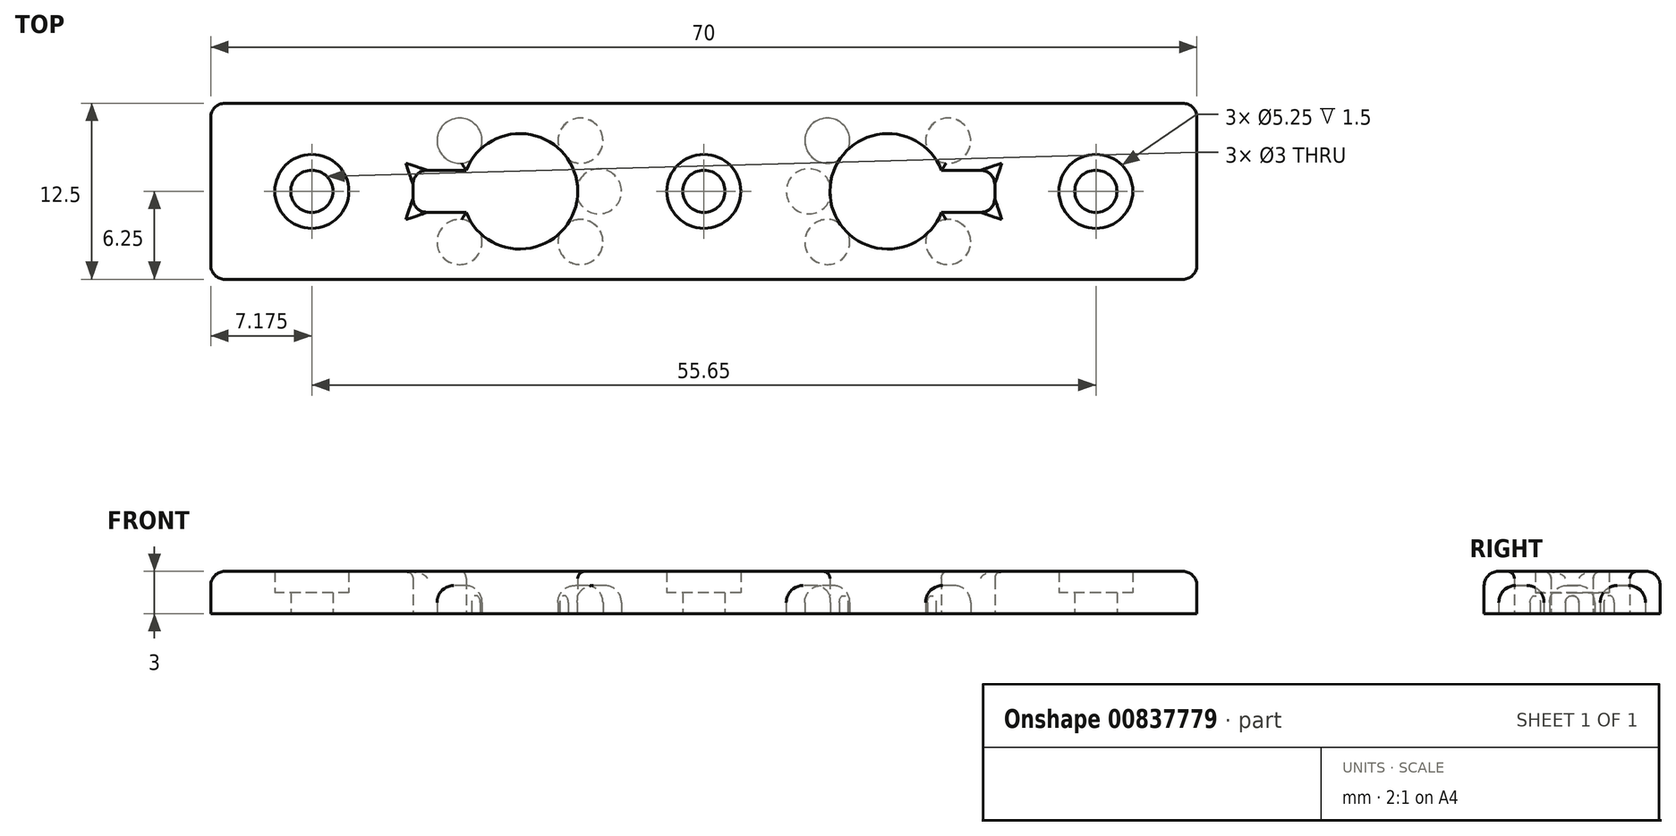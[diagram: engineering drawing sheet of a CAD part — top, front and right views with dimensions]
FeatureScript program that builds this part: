
annotation { "Feature Type Name" : "Feature", "Feature Type Description" : "" }
export const myFeature = defineFeature(function(context is Context, id is Id, definition is map)
    precondition{}
    {
        {
            var Q0;
            Q0=qCreatedBy(makeId("Top.planeOp"),FACE);
            var sketch = newSketch(context, id + "F0", { "sketchPlane" : qUnion([Q0])});
            skLineSegment(sketch, "E0.bottom", {"start": v(35, 6.25) * mm, "end": v(-35, 6.25) * mm});
            skLineSegment(sketch, "E0.top", {"start": v(35, -6.25) * mm, "end": v(-35, -6.25) * mm});
            skLineSegment(sketch, "E0.left", {"start": v(35, 6.25) * mm, "end": v(35, -6.25) * mm});
            skLineSegment(sketch, "E0.right", {"start": v(-35, 6.25) * mm, "end": v(-35, -6.25) * mm});
            skPoint(sketch, "E0.middle", {"position": v(0, 0) * mm});
            skLineSegment(sketch, "E1", {"start": v(-35, 0) * mm, "end": v(-13.05, 0) * mm, "construction": true});
            skLineSegment(sketch, "E2", {"start": v(35, 0) * mm, "end": v(13.05, 0) * mm, "construction": true});
            skCircle(sketch, "E3", {"center": v(-13.05, 0) * mm, "radius": 4.1 * mm});
            skCircle(sketch, "E4", {"center": v(13.05, 0) * mm, "radius": 4.1 * mm});
            skLineSegment(sketch, "E5", {"start": v(-13.05, 0) * mm, "end": v(-8.95, 0) * mm, "construction": true});
            skLineSegment(sketch, "E6", {"start": v(-16.2, 2.64) * mm, "end": v(-13.05, 0) * mm, "construction": true});
            skCircle(sketch, "E7", {"center": v(-13.05, 0) * mm, "radius": 4 * mm, "construction": true});
            skLineSegment(sketch, "E8", {"start": v(-17.15, 0) * mm, "end": v(-20.65, 0) * mm, "construction": true});
            skLineSegment(sketch, "E9", {"start": v(-20.65, 0) * mm, "end": v(-20.65, 1.5) * mm});
            skLineSegment(sketch, "E10", {"start": v(-20.65, 0) * mm, "end": v(-20.65, -1.5) * mm});
            skLineSegment(sketch, "E11", {"start": v(-20.65, 1.5) * mm, "end": v(-16.87, 1.5) * mm});
            skLineSegment(sketch, "E12", {"start": v(-20.65, -1.5) * mm, "end": v(-16.87, -1.5) * mm});
            skLineSegment(sketch, "E13", {"start": v(17.15, 0) * mm, "end": v(20.65, 0) * mm, "construction": true});
            skLineSegment(sketch, "E14", {"start": v(20.65, 0) * mm, "end": v(20.65, 1.5) * mm});
            skLineSegment(sketch, "E15", {"start": v(20.65, 1.5) * mm, "end": v(16.87, 1.5) * mm});
            skLineSegment(sketch, "E16", {"start": v(20.65, 0) * mm, "end": v(20.65, -1.5) * mm});
            skLineSegment(sketch, "E17", {"start": v(20.65, -1.5) * mm, "end": v(16.87, -1.5) * mm});
            skCircle(sketch, "E18", {"center": v(0, 0) * mm, "radius": 1.5 * mm});
            skLineSegment(sketch, "E19", {"start": v(-35, 0) * mm, "end": v(-27.83, 0) * mm, "construction": true});
            skLineSegment(sketch, "E20", {"start": v(35, 0) * mm, "end": v(27.83, 0) * mm, "construction": true});
            skCircle(sketch, "E21", {"center": v(27.83, 0) * mm, "radius": 1.5 * mm});
            skCircle(sketch, "E22", {"center": v(-27.83, 0) * mm, "radius": 1.5 * mm});
            skCircle(sketch, "E23", {"center": v(-27.83, 0) * mm, "radius": 2.62 * mm});
            skCircle(sketch, "E24", {"center": v(0, 0) * mm, "radius": 2.62 * mm});
            skCircle(sketch, "E25", {"center": v(27.83, 0) * mm, "radius": 2.62 * mm});
            skLineSegment(sketch, "E26", {"start": v(-16.11, 2.57) * mm, "end": v(-16.78, 3.13) * mm, "construction": true});
            skLineSegment(sketch, "E27", {"start": v(-16.11, -2.57) * mm, "end": v(-16.78, -3.13) * mm, "construction": true});
            skCircle(sketch, "E28", {"center": v(-16.78, -3.13) * mm, "radius": 0.88 * mm});
            skCircle(sketch, "E29", {"center": v(-16.78, 3.13) * mm, "radius": 0.88 * mm});
            skLineSegment(sketch, "E30", {"start": v(-13.05, 0) * mm, "end": v(-9.9, 2.64) * mm, "construction": true});
            skLineSegment(sketch, "E31", {"start": v(-13.05, 0) * mm, "end": v(-17.15, 0) * mm, "construction": true});
            skLineSegment(sketch, "E32", {"start": v(-13.05, 0) * mm, "end": v(-9.9, -2.64) * mm, "construction": true});
            skLineSegment(sketch, "E33", {"start": v(-9.99, 2.57) * mm, "end": v(-9.32, 3.13) * mm, "construction": true});
            skLineSegment(sketch, "E34", {"start": v(-9.99, -2.57) * mm, "end": v(-9.32, -3.13) * mm, "construction": true});
            skCircle(sketch, "E35", {"center": v(-9.32, -3.13) * mm, "radius": 0.88 * mm});
            skCircle(sketch, "E36", {"center": v(-9.32, 3.13) * mm, "radius": 0.88 * mm});
            skLineSegment(sketch, "E37", {"start": v(-9.05, 0) * mm, "end": v(-8.18, 0) * mm, "construction": true});
            skCircle(sketch, "E38", {"center": v(-8.18, 0) * mm, "radius": 0.88 * mm});
            skLineSegment(sketch, "E39", {"start": v(13.05, 0) * mm, "end": v(8.95, 0) * mm, "construction": true});
            skCircle(sketch, "E40", {"center": v(13.05, 0) * mm, "radius": 4 * mm, "construction": true});
            skLineSegment(sketch, "E41", {"start": v(16.11, 2.57) * mm, "end": v(16.78, 3.13) * mm, "construction": true});
            skLineSegment(sketch, "E42", {"start": v(16.11, -2.57) * mm, "end": v(16.78, -3.13) * mm, "construction": true});
            skLineSegment(sketch, "E43", {"start": v(9.05, 0) * mm, "end": v(8.18, 0) * mm, "construction": true});
            skCircle(sketch, "E44", {"center": v(8.18, 0) * mm, "radius": 0.88 * mm});
            skCircle(sketch, "E45", {"center": v(16.78, 3.13) * mm, "radius": 0.88 * mm});
            skCircle(sketch, "E46", {"center": v(16.78, -3.13) * mm, "radius": 0.88 * mm});
            skLineSegment(sketch, "E47", {"start": v(13.05, 0) * mm, "end": v(9.9, 2.64) * mm, "construction": true});
            skLineSegment(sketch, "E48", {"start": v(9.9, -2.64) * mm, "end": v(13.05, 0) * mm, "construction": true});
            skLineSegment(sketch, "E49", {"start": v(9.99, 2.57) * mm, "end": v(9.32, 3.13) * mm, "construction": true});
            skLineSegment(sketch, "E50", {"start": v(9.99, -2.57) * mm, "end": v(9.32, -3.13) * mm, "construction": true});
            skCircle(sketch, "E51", {"center": v(9.32, 3.13) * mm, "radius": 0.88 * mm});
            skCircle(sketch, "E52", {"center": v(9.32, -3.13) * mm, "radius": 0.88 * mm});
            skLineSegment(sketch, "E53", {"start": v(-16.11, -2.57) * mm, "end": v(-17.34, -3.6) * mm, "construction": true});
            skLineSegment(sketch, "E54", {"start": v(-9.99, -2.57) * mm, "end": v(-8.76, -3.6) * mm, "construction": true});
            skLineSegment(sketch, "E55", {"start": v(-9.05, 0) * mm, "end": v(-7.45, 0) * mm, "construction": true});
            skLineSegment(sketch, "E56", {"start": v(-9.99, 2.57) * mm, "end": v(-8.76, 3.6) * mm, "construction": true});
            skLineSegment(sketch, "E57", {"start": v(-16.11, 2.57) * mm, "end": v(-17.34, 3.6) * mm, "construction": true});
            skCircle(sketch, "E58", {"center": v(-17.34, -3.6) * mm, "radius": 1.6 * mm});
            skCircle(sketch, "E59", {"center": v(-8.76, -3.6) * mm, "radius": 1.6 * mm});
            skCircle(sketch, "E60", {"center": v(-7.45, 0) * mm, "radius": 1.6 * mm});
            skCircle(sketch, "E61", {"center": v(-8.76, 3.6) * mm, "radius": 1.6 * mm});
            skCircle(sketch, "E62", {"center": v(-17.34, 3.6) * mm, "radius": 1.6 * mm});
            skLineSegment(sketch, "E63", {"start": v(9.99, -2.57) * mm, "end": v(8.76, -3.6) * mm, "construction": true});
            skLineSegment(sketch, "E64", {"start": v(9.05, 0) * mm, "end": v(7.45, 0) * mm, "construction": true});
            skLineSegment(sketch, "E65", {"start": v(9.99, 2.57) * mm, "end": v(8.76, 3.6) * mm, "construction": true});
            skLineSegment(sketch, "E66", {"start": v(16.11, 2.57) * mm, "end": v(17.34, 3.6) * mm, "construction": true});
            skLineSegment(sketch, "E67", {"start": v(16.11, -2.57) * mm, "end": v(17.34, -3.6) * mm, "construction": true});
            skCircle(sketch, "E68", {"center": v(8.76, -3.6) * mm, "radius": 1.6 * mm});
            skCircle(sketch, "E69", {"center": v(7.45, 0) * mm, "radius": 1.6 * mm});
            skCircle(sketch, "E70", {"center": v(8.76, 3.6) * mm, "radius": 1.6 * mm});
            skCircle(sketch, "E71", {"center": v(17.34, 3.6) * mm, "radius": 1.6 * mm});
            skCircle(sketch, "E72", {"center": v(17.34, -3.6) * mm, "radius": 1.6 * mm});
            skSolve(sketch);
        }
        {
            var Q0;
            Q0=makeQuery(id+"F0.imprint","IMPRINT",FACE,{"disambiguationData":[TD([[makeQuery(id+"F0.imprint","IMPRINT",EDGE,{"derivedFrom":sQuery(id+"F0.wireOp",EDGE,"E0.bottom")}),1.0]])]});
            var Q1;
            Q1=makeQuery(id+"F0.imprint","IMPRINT",FACE,{"disambiguationData":[TD([[makeQuery(id+"F0.imprint","IMPRINT",EDGE,{"derivedFrom":sQuery(id+"F0.wireOp",EDGE,"E18")}),-1.0]])]});
            var Q2;
            Q2=makeQuery(id+"F0.imprint","IMPRINT",FACE,{"disambiguationData":[TD([[makeQuery(id+"F0.imprint","IMPRINT",EDGE,{"derivedFrom":sQuery(id+"F0.wireOp",EDGE,"E22")}),-1.0]])]});
            var Q3;
            Q3=makeQuery(id+"F0.imprint","IMPRINT",FACE,{"disambiguationData":[TD([[makeQuery(id+"F0.imprint","IMPRINT",EDGE,{"derivedFrom":sQuery(id+"F0.wireOp",EDGE,"E21")}),-1.0]])]});
            var Q4;
            {var subQ0=sQuery(id+"F0.wireOp",EDGE,"E29");var subQ1=sQuery(id+"F0.wireOp",EDGE,"E3");var subQ2=makeQuery(id+"F0.imprint","INTERSECT",VERTEX,{"disambiguationData":[OD(0.0)],"derivedFrom":[subQ1,subQ0]});Q4=makeQuery(id+"F0.imprint","IMPRINT",FACE,{"disambiguationData":[TD([[makeQuery(id+"F0.imprint","IMPRINT",EDGE,{"disambiguationData":[TD([[subQ2,-1.0]])],"derivedFrom":subQ1}),-1.0]])]});}
            var Q5;
            {var subQ0=sQuery(id+"F0.wireOp",EDGE,"E36");var subQ1=sQuery(id+"F0.wireOp",EDGE,"E3");var subQ2=makeQuery(id+"F0.imprint","INTERSECT",VERTEX,{"disambiguationData":[OD(0.0)],"derivedFrom":[subQ1,subQ0]});Q5=makeQuery(id+"F0.imprint","IMPRINT",FACE,{"disambiguationData":[TD([[makeQuery(id+"F0.imprint","IMPRINT",EDGE,{"disambiguationData":[TD([[subQ2,-1.0]])],"derivedFrom":subQ1}),-1.0]])]});}
            var Q6;
            {var subQ0=sQuery(id+"F0.wireOp",EDGE,"E38");var subQ1=sQuery(id+"F0.wireOp",EDGE,"E3");var subQ2=makeQuery(id+"F0.imprint","INTERSECT",VERTEX,{"disambiguationData":[OD(0.0)],"derivedFrom":[subQ1,subQ0]});Q6=makeQuery(id+"F0.imprint","IMPRINT",FACE,{"disambiguationData":[TD([[makeQuery(id+"F0.imprint","IMPRINT",EDGE,{"disambiguationData":[TD([[subQ2,1.0]])],"derivedFrom":subQ1}),-1.0]])]});}
            var Q7;
            {var subQ0=sQuery(id+"F0.wireOp",EDGE,"E28");var subQ1=sQuery(id+"F0.wireOp",EDGE,"E3");var subQ2=makeQuery(id+"F0.imprint","INTERSECT",VERTEX,{"disambiguationData":[OD(0.0)],"derivedFrom":[subQ1,subQ0]});Q7=makeQuery(id+"F0.imprint","IMPRINT",FACE,{"disambiguationData":[TD([[makeQuery(id+"F0.imprint","IMPRINT",EDGE,{"disambiguationData":[TD([[subQ2,-1.0]])],"derivedFrom":subQ1}),-1.0]])]});}
            var Q8;
            {var subQ0=sQuery(id+"F0.wireOp",EDGE,"E35");var subQ1=sQuery(id+"F0.wireOp",EDGE,"E3");var subQ2=makeQuery(id+"F0.imprint","INTERSECT",VERTEX,{"disambiguationData":[OD(0.0)],"derivedFrom":[subQ1,subQ0]});Q8=makeQuery(id+"F0.imprint","IMPRINT",FACE,{"disambiguationData":[TD([[makeQuery(id+"F0.imprint","IMPRINT",EDGE,{"disambiguationData":[TD([[subQ2,-1.0]])],"derivedFrom":subQ1}),-1.0]])]});}
            var Q9;
            {var subQ0=sQuery(id+"F0.wireOp",EDGE,"E51");var subQ1=sQuery(id+"F0.wireOp",EDGE,"E4");var subQ2=makeQuery(id+"F0.imprint","INTERSECT",VERTEX,{"disambiguationData":[OD(0.0)],"derivedFrom":[subQ1,subQ0]});Q9=makeQuery(id+"F0.imprint","IMPRINT",FACE,{"disambiguationData":[TD([[makeQuery(id+"F0.imprint","IMPRINT",EDGE,{"disambiguationData":[TD([[subQ2,-1.0]])],"derivedFrom":subQ1}),-1.0]])]});}
            var Q10;
            {var subQ0=sQuery(id+"F0.wireOp",EDGE,"E44");var subQ1=sQuery(id+"F0.wireOp",EDGE,"E4");var subQ2=makeQuery(id+"F0.imprint","INTERSECT",VERTEX,{"disambiguationData":[OD(0.0)],"derivedFrom":[subQ1,subQ0]});Q10=makeQuery(id+"F0.imprint","IMPRINT",FACE,{"disambiguationData":[TD([[makeQuery(id+"F0.imprint","IMPRINT",EDGE,{"disambiguationData":[TD([[subQ2,-1.0]])],"derivedFrom":subQ1}),-1.0]])]});}
            var Q11;
            {var subQ0=sQuery(id+"F0.wireOp",EDGE,"E52");var subQ1=sQuery(id+"F0.wireOp",EDGE,"E4");var subQ2=makeQuery(id+"F0.imprint","INTERSECT",VERTEX,{"disambiguationData":[OD(0.0)],"derivedFrom":[subQ1,subQ0]});Q11=makeQuery(id+"F0.imprint","IMPRINT",FACE,{"disambiguationData":[TD([[makeQuery(id+"F0.imprint","IMPRINT",EDGE,{"disambiguationData":[TD([[subQ2,-1.0]])],"derivedFrom":subQ1}),-1.0]])]});}
            var Q12;
            {var subQ0=sQuery(id+"F0.wireOp",EDGE,"E46");var subQ1=sQuery(id+"F0.wireOp",EDGE,"E4");var subQ2=makeQuery(id+"F0.imprint","INTERSECT",VERTEX,{"disambiguationData":[OD(0.0)],"derivedFrom":[subQ1,subQ0]});Q12=makeQuery(id+"F0.imprint","IMPRINT",FACE,{"disambiguationData":[TD([[makeQuery(id+"F0.imprint","IMPRINT",EDGE,{"disambiguationData":[TD([[subQ2,-1.0]])],"derivedFrom":subQ1}),-1.0]])]});}
            var Q13;
            {var subQ0=sQuery(id+"F0.wireOp",EDGE,"E45");var subQ1=sQuery(id+"F0.wireOp",EDGE,"E4");var subQ2=makeQuery(id+"F0.imprint","INTERSECT",VERTEX,{"disambiguationData":[OD(0.0)],"derivedFrom":[subQ1,subQ0]});Q13=makeQuery(id+"F0.imprint","IMPRINT",FACE,{"disambiguationData":[TD([[makeQuery(id+"F0.imprint","IMPRINT",EDGE,{"disambiguationData":[TD([[subQ2,-1.0]])],"derivedFrom":subQ1}),-1.0]])]});}
            var Q14;
            {var subQ0=sQuery(id+"F0.wireOp",EDGE,"VOKNR2WF-ncJ6-5r4m-VKTM-Mp244crdFX1A");var subQ1=sQuery(id+"F0.wireOp",EDGE,"E4");var subQ2=makeQuery(id+"F0.imprint","INTERSECT",VERTEX,{"disambiguationData":[OD(0.0)],"derivedFrom":[subQ1,subQ0]});Q14=makeQuery(id+"F0.imprint","IMPRINT",FACE,{"disambiguationData":[TD([[makeQuery(id+"F0.imprint","IMPRINT",EDGE,{"disambiguationData":[TD([[subQ2,-1.0]])],"derivedFrom":subQ1}),-1.0]])]});}
            var Q15;
            {var subQ0=sQuery(id+"F0.wireOp",EDGE,"JKFwxpca-5GMR-r81S-5lcH-Q0wAUQQhRcdb");var subQ1=sQuery(id+"F0.wireOp",EDGE,"E4");var subQ2=makeQuery(id+"F0.imprint","INTERSECT",VERTEX,{"disambiguationData":[OD(0.0)],"derivedFrom":[subQ1,subQ0]});Q15=makeQuery(id+"F0.imprint","IMPRINT",FACE,{"disambiguationData":[TD([[makeQuery(id+"F0.imprint","IMPRINT",EDGE,{"disambiguationData":[TD([[subQ2,-1.0]])],"derivedFrom":subQ1}),-1.0]])]});}
            var Q16;
            {var subQ0=sQuery(id+"F0.wireOp",EDGE,"RgAsl8GP-AyME-5KkZ-DOE9-8E78qrft6pB6");var subQ1=sQuery(id+"F0.wireOp",EDGE,"E4");var subQ2=makeQuery(id+"F0.imprint","INTERSECT",VERTEX,{"disambiguationData":[OD(0.0)],"derivedFrom":[subQ1,subQ0]});Q16=makeQuery(id+"F0.imprint","IMPRINT",FACE,{"disambiguationData":[TD([[makeQuery(id+"F0.imprint","IMPRINT",EDGE,{"disambiguationData":[TD([[subQ2,-1.0]])],"derivedFrom":subQ1}),-1.0]])]});}
            var Q17;
            {var subQ0=sQuery(id+"F0.wireOp",EDGE,"FUVbCvpG-FZ6w-P6KP-I0dI-AxA5oCcrSkfj");var subQ1=sQuery(id+"F0.wireOp",EDGE,"E4");var subQ2=makeQuery(id+"F0.imprint","INTERSECT",VERTEX,{"disambiguationData":[OD(0.0)],"derivedFrom":[subQ1,subQ0]});Q17=makeQuery(id+"F0.imprint","IMPRINT",FACE,{"disambiguationData":[TD([[makeQuery(id+"F0.imprint","IMPRINT",EDGE,{"disambiguationData":[TD([[subQ2,-1.0]])],"derivedFrom":subQ1}),-1.0]])]});}
            var Q18;
            {var subQ0=sQuery(id+"F0.wireOp",EDGE,"rxho1QIs-J72r-V1yP-Fany-Pfa95wKSQuel");var subQ1=sQuery(id+"F0.wireOp",EDGE,"E4");var subQ2=makeQuery(id+"F0.imprint","INTERSECT",VERTEX,{"disambiguationData":[OD(0.0)],"derivedFrom":[subQ1,subQ0]});Q18=makeQuery(id+"F0.imprint","IMPRINT",FACE,{"disambiguationData":[TD([[makeQuery(id+"F0.imprint","IMPRINT",EDGE,{"disambiguationData":[TD([[subQ2,-1.0]])],"derivedFrom":subQ1}),-1.0]])]});}
            var Q19;
            {var subQ0=sQuery(id+"F0.wireOp",EDGE,"6oBsojoL-bi50-brXo-pCNQ-iNl1vZV5s9Sy");var subQ1=sQuery(id+"F0.wireOp",EDGE,"E3");var subQ2=makeQuery(id+"F0.imprint","INTERSECT",VERTEX,{"disambiguationData":[OD(0.0)],"derivedFrom":[subQ1,subQ0]});Q19=makeQuery(id+"F0.imprint","IMPRINT",FACE,{"disambiguationData":[TD([[makeQuery(id+"F0.imprint","IMPRINT",EDGE,{"disambiguationData":[TD([[subQ2,-1.0]])],"derivedFrom":subQ1}),-1.0]])]});}
            var Q20;
            {var subQ0=sQuery(id+"F0.wireOp",EDGE,"yIff1Jyh-36eP-EJu2-z3IG-mIHMmL8X11wQ");var subQ1=sQuery(id+"F0.wireOp",EDGE,"E3");var subQ2=makeQuery(id+"F0.imprint","INTERSECT",VERTEX,{"disambiguationData":[OD(0.0)],"derivedFrom":[subQ1,subQ0]});Q20=makeQuery(id+"F0.imprint","IMPRINT",FACE,{"disambiguationData":[TD([[makeQuery(id+"F0.imprint","IMPRINT",EDGE,{"disambiguationData":[TD([[subQ2,-1.0]])],"derivedFrom":subQ1}),-1.0]])]});}
            var Q21;
            {var subQ0=sQuery(id+"F0.wireOp",EDGE,"BIAei6Qo-JPVI-veR3-2g77-xNxDojE5xRzN");var subQ1=sQuery(id+"F0.wireOp",EDGE,"E3");var subQ2=makeQuery(id+"F0.imprint","INTERSECT",VERTEX,{"disambiguationData":[OD(0.0)],"derivedFrom":[subQ1,subQ0]});Q21=makeQuery(id+"F0.imprint","IMPRINT",FACE,{"disambiguationData":[TD([[makeQuery(id+"F0.imprint","IMPRINT",EDGE,{"disambiguationData":[TD([[subQ2,-1.0]])],"derivedFrom":subQ1}),-1.0]])]});}
            var Q22;
            {var subQ0=sQuery(id+"F0.wireOp",EDGE,"AHdYGSoF-gAz6-Gu7A-dCm8-YOlxFVZfYSgz");var subQ1=sQuery(id+"F0.wireOp",EDGE,"E3");var subQ2=makeQuery(id+"F0.imprint","INTERSECT",VERTEX,{"disambiguationData":[OD(0.0)],"derivedFrom":[subQ1,subQ0]});Q22=makeQuery(id+"F0.imprint","IMPRINT",FACE,{"disambiguationData":[TD([[makeQuery(id+"F0.imprint","IMPRINT",EDGE,{"disambiguationData":[TD([[subQ2,-1.0]])],"derivedFrom":subQ1}),-1.0]])]});}
            var Q23;
            {var subQ0=sQuery(id+"F0.wireOp",EDGE,"bF5o1xas-ZAw9-uCyn-oNpS-FKpWy39mbc2z");var subQ1=sQuery(id+"F0.wireOp",EDGE,"E3");var subQ2=makeQuery(id+"F0.imprint","INTERSECT",VERTEX,{"disambiguationData":[OD(0.0)],"derivedFrom":[subQ1,subQ0]});Q23=makeQuery(id+"F0.imprint","IMPRINT",FACE,{"disambiguationData":[TD([[makeQuery(id+"F0.imprint","IMPRINT",EDGE,{"disambiguationData":[TD([[subQ2,1.0]])],"derivedFrom":subQ1}),-1.0]])]});}
            var Q24;
            {var subQ0=sQuery(id+"F0.wireOp",EDGE,"E69");var subQ1=sQuery(id+"F0.wireOp",EDGE,"E4");var subQ2=makeQuery(id+"F0.imprint","INTERSECT",VERTEX,{"disambiguationData":[OD(0.0)],"derivedFrom":[subQ1,subQ0]});Q24=makeQuery(id+"F0.imprint","IMPRINT",FACE,{"disambiguationData":[TD([[makeQuery(id+"F0.imprint","IMPRINT",EDGE,{"disambiguationData":[TD([[subQ2,-1.0]])],"derivedFrom":subQ1}),-1.0]])]});}
            var Q25;
            {var subQ0=sQuery(id+"F0.wireOp",EDGE,"E68");var subQ1=sQuery(id+"F0.wireOp",EDGE,"E4");var subQ2=makeQuery(id+"F0.imprint","INTERSECT",VERTEX,{"disambiguationData":[OD(0.0)],"derivedFrom":[subQ1,subQ0]});Q25=makeQuery(id+"F0.imprint","IMPRINT",FACE,{"disambiguationData":[TD([[makeQuery(id+"F0.imprint","IMPRINT",EDGE,{"disambiguationData":[TD([[subQ2,-1.0]])],"derivedFrom":subQ1}),-1.0]])]});}
            var Q26;
            {var subQ0=sQuery(id+"F0.wireOp",EDGE,"E72");var subQ1=sQuery(id+"F0.wireOp",EDGE,"E4");var subQ2=makeQuery(id+"F0.imprint","INTERSECT",VERTEX,{"disambiguationData":[OD(0.0)],"derivedFrom":[subQ1,subQ0]});Q26=makeQuery(id+"F0.imprint","IMPRINT",FACE,{"disambiguationData":[TD([[makeQuery(id+"F0.imprint","IMPRINT",EDGE,{"disambiguationData":[TD([[subQ2,-1.0]])],"derivedFrom":subQ1}),-1.0]])]});}
            var Q27;
            {var subQ0=sQuery(id+"F0.wireOp",EDGE,"E71");var subQ1=sQuery(id+"F0.wireOp",EDGE,"E4");var subQ2=makeQuery(id+"F0.imprint","INTERSECT",VERTEX,{"disambiguationData":[OD(0.0)],"derivedFrom":[subQ1,subQ0]});Q27=makeQuery(id+"F0.imprint","IMPRINT",FACE,{"disambiguationData":[TD([[makeQuery(id+"F0.imprint","IMPRINT",EDGE,{"disambiguationData":[TD([[subQ2,-1.0]])],"derivedFrom":subQ1}),-1.0]])]});}
            var Q28;
            {var subQ0=sQuery(id+"F0.wireOp",EDGE,"E70");var subQ1=sQuery(id+"F0.wireOp",EDGE,"E4");var subQ2=makeQuery(id+"F0.imprint","INTERSECT",VERTEX,{"disambiguationData":[OD(0.0)],"derivedFrom":[subQ1,subQ0]});Q28=makeQuery(id+"F0.imprint","IMPRINT",FACE,{"disambiguationData":[TD([[makeQuery(id+"F0.imprint","IMPRINT",EDGE,{"disambiguationData":[TD([[subQ2,-1.0]])],"derivedFrom":subQ1}),-1.0]])]});}
            var Q29;
            {var subQ0=sQuery(id+"F0.wireOp",EDGE,"E58");var subQ1=sQuery(id+"F0.wireOp",EDGE,"E3");var subQ2=makeQuery(id+"F0.imprint","INTERSECT",VERTEX,{"disambiguationData":[OD(0.0)],"derivedFrom":[subQ1,subQ0]});Q29=makeQuery(id+"F0.imprint","IMPRINT",FACE,{"disambiguationData":[TD([[makeQuery(id+"F0.imprint","IMPRINT",EDGE,{"disambiguationData":[TD([[subQ2,-1.0]])],"derivedFrom":subQ1}),-1.0]])]});}
            var Q30;
            {var subQ0=sQuery(id+"F0.wireOp",EDGE,"E62");var subQ1=sQuery(id+"F0.wireOp",EDGE,"E3");var subQ2=makeQuery(id+"F0.imprint","INTERSECT",VERTEX,{"disambiguationData":[OD(0.0)],"derivedFrom":[subQ1,subQ0]});Q30=makeQuery(id+"F0.imprint","IMPRINT",FACE,{"disambiguationData":[TD([[makeQuery(id+"F0.imprint","IMPRINT",EDGE,{"disambiguationData":[TD([[subQ2,-1.0]])],"derivedFrom":subQ1}),-1.0]])]});}
            var Q31;
            {var subQ0=sQuery(id+"F0.wireOp",EDGE,"E61");var subQ1=sQuery(id+"F0.wireOp",EDGE,"E3");var subQ2=makeQuery(id+"F0.imprint","INTERSECT",VERTEX,{"disambiguationData":[OD(0.0)],"derivedFrom":[subQ1,subQ0]});Q31=makeQuery(id+"F0.imprint","IMPRINT",FACE,{"disambiguationData":[TD([[makeQuery(id+"F0.imprint","IMPRINT",EDGE,{"disambiguationData":[TD([[subQ2,-1.0]])],"derivedFrom":subQ1}),-1.0]])]});}
            var Q32;
            {var subQ0=sQuery(id+"F0.wireOp",EDGE,"E60");var subQ1=sQuery(id+"F0.wireOp",EDGE,"E3");var subQ2=makeQuery(id+"F0.imprint","INTERSECT",VERTEX,{"disambiguationData":[OD(0.0)],"derivedFrom":[subQ1,subQ0]});Q32=makeQuery(id+"F0.imprint","IMPRINT",FACE,{"disambiguationData":[TD([[makeQuery(id+"F0.imprint","IMPRINT",EDGE,{"disambiguationData":[TD([[subQ2,1.0]])],"derivedFrom":subQ1}),-1.0]])]});}
            var Q33;
            {var subQ0=sQuery(id+"F0.wireOp",EDGE,"E59");var subQ1=sQuery(id+"F0.wireOp",EDGE,"E3");var subQ2=makeQuery(id+"F0.imprint","INTERSECT",VERTEX,{"disambiguationData":[OD(0.0)],"derivedFrom":[subQ1,subQ0]});Q33=makeQuery(id+"F0.imprint","IMPRINT",FACE,{"disambiguationData":[TD([[makeQuery(id+"F0.imprint","IMPRINT",EDGE,{"disambiguationData":[TD([[subQ2,-1.0]])],"derivedFrom":subQ1}),-1.0]])]});}
            extrude(context, id + "F1", {"entities" : qUnion([Q0, Q1, Q2, Q3, Q4, Q5, Q6, Q7, Q8, Q9, Q10, Q11, Q12, Q13, Q14, Q15, Q16, Q17, Q18, Q19, Q20, Q21, Q22, Q23, Q24, Q25, Q26, Q27, Q28, Q29, Q30, Q31, Q32, Q33]), "depth" : 3 * mm, "offsetDistance" : 25 * mm});
        }
        {
            var Q0;
            {var subQ0=sQuery(id+"F0.wireOp",EDGE,"E28");var subQ1=sQuery(id+"F0.wireOp",EDGE,"E3");var subQ2=makeQuery(id+"F0.imprint","INTERSECT",VERTEX,{"disambiguationData":[OD(0.0)],"derivedFrom":[subQ1,subQ0]});Q0=makeQuery(id+"F0.imprint","IMPRINT",FACE,{"disambiguationData":[TD([[makeQuery(id+"F0.imprint","IMPRINT",EDGE,{"disambiguationData":[TD([[subQ2,-1.0]])],"derivedFrom":subQ1}),-1.0]])]});}
            var Q1;
            {var subQ0=sQuery(id+"F0.wireOp",EDGE,"E29");var subQ1=sQuery(id+"F0.wireOp",EDGE,"E3");var subQ2=makeQuery(id+"F0.imprint","INTERSECT",VERTEX,{"disambiguationData":[OD(0.0)],"derivedFrom":[subQ1,subQ0]});Q1=makeQuery(id+"F0.imprint","IMPRINT",FACE,{"disambiguationData":[TD([[makeQuery(id+"F0.imprint","IMPRINT",EDGE,{"disambiguationData":[TD([[subQ2,-1.0]])],"derivedFrom":subQ1}),-1.0]])]});}
            var Q2;
            {var subQ0=sQuery(id+"F0.wireOp",EDGE,"E36");var subQ1=sQuery(id+"F0.wireOp",EDGE,"E3");var subQ2=makeQuery(id+"F0.imprint","INTERSECT",VERTEX,{"disambiguationData":[OD(0.0)],"derivedFrom":[subQ1,subQ0]});Q2=makeQuery(id+"F0.imprint","IMPRINT",FACE,{"disambiguationData":[TD([[makeQuery(id+"F0.imprint","IMPRINT",EDGE,{"disambiguationData":[TD([[subQ2,-1.0]])],"derivedFrom":subQ1}),-1.0]])]});}
            var Q3;
            {var subQ0=sQuery(id+"F0.wireOp",EDGE,"E38");var subQ1=sQuery(id+"F0.wireOp",EDGE,"E3");var subQ2=makeQuery(id+"F0.imprint","INTERSECT",VERTEX,{"disambiguationData":[OD(0.0)],"derivedFrom":[subQ1,subQ0]});Q3=makeQuery(id+"F0.imprint","IMPRINT",FACE,{"disambiguationData":[TD([[makeQuery(id+"F0.imprint","IMPRINT",EDGE,{"disambiguationData":[TD([[subQ2,1.0]])],"derivedFrom":subQ1}),-1.0]])]});}
            var Q4;
            {var subQ0=sQuery(id+"F0.wireOp",EDGE,"E35");var subQ1=sQuery(id+"F0.wireOp",EDGE,"E3");var subQ2=makeQuery(id+"F0.imprint","INTERSECT",VERTEX,{"disambiguationData":[OD(0.0)],"derivedFrom":[subQ1,subQ0]});Q4=makeQuery(id+"F0.imprint","IMPRINT",FACE,{"disambiguationData":[TD([[makeQuery(id+"F0.imprint","IMPRINT",EDGE,{"disambiguationData":[TD([[subQ2,-1.0]])],"derivedFrom":subQ1}),-1.0]])]});}
            var Q5;
            {var subQ0=sQuery(id+"F0.wireOp",EDGE,"E52");var subQ1=sQuery(id+"F0.wireOp",EDGE,"E4");var subQ2=makeQuery(id+"F0.imprint","INTERSECT",VERTEX,{"disambiguationData":[OD(0.0)],"derivedFrom":[subQ1,subQ0]});Q5=makeQuery(id+"F0.imprint","IMPRINT",FACE,{"disambiguationData":[TD([[makeQuery(id+"F0.imprint","IMPRINT",EDGE,{"disambiguationData":[TD([[subQ2,-1.0]])],"derivedFrom":subQ1}),-1.0]])]});}
            var Q6;
            {var subQ0=sQuery(id+"F0.wireOp",EDGE,"E44");var subQ1=sQuery(id+"F0.wireOp",EDGE,"E4");var subQ2=makeQuery(id+"F0.imprint","INTERSECT",VERTEX,{"disambiguationData":[OD(0.0)],"derivedFrom":[subQ1,subQ0]});Q6=makeQuery(id+"F0.imprint","IMPRINT",FACE,{"disambiguationData":[TD([[makeQuery(id+"F0.imprint","IMPRINT",EDGE,{"disambiguationData":[TD([[subQ2,-1.0]])],"derivedFrom":subQ1}),-1.0]])]});}
            var Q7;
            {var subQ0=sQuery(id+"F0.wireOp",EDGE,"E51");var subQ1=sQuery(id+"F0.wireOp",EDGE,"E4");var subQ2=makeQuery(id+"F0.imprint","INTERSECT",VERTEX,{"disambiguationData":[OD(0.0)],"derivedFrom":[subQ1,subQ0]});Q7=makeQuery(id+"F0.imprint","IMPRINT",FACE,{"disambiguationData":[TD([[makeQuery(id+"F0.imprint","IMPRINT",EDGE,{"disambiguationData":[TD([[subQ2,-1.0]])],"derivedFrom":subQ1}),-1.0]])]});}
            var Q8;
            {var subQ0=sQuery(id+"F0.wireOp",EDGE,"E46");var subQ1=sQuery(id+"F0.wireOp",EDGE,"E4");var subQ2=makeQuery(id+"F0.imprint","INTERSECT",VERTEX,{"disambiguationData":[OD(0.0)],"derivedFrom":[subQ1,subQ0]});Q8=makeQuery(id+"F0.imprint","IMPRINT",FACE,{"disambiguationData":[TD([[makeQuery(id+"F0.imprint","IMPRINT",EDGE,{"disambiguationData":[TD([[subQ2,-1.0]])],"derivedFrom":subQ1}),-1.0]])]});}
            var Q9;
            {var subQ0=sQuery(id+"F0.wireOp",EDGE,"E45");var subQ1=sQuery(id+"F0.wireOp",EDGE,"E4");var subQ2=makeQuery(id+"F0.imprint","INTERSECT",VERTEX,{"disambiguationData":[OD(0.0)],"derivedFrom":[subQ1,subQ0]});Q9=makeQuery(id+"F0.imprint","IMPRINT",FACE,{"disambiguationData":[TD([[makeQuery(id+"F0.imprint","IMPRINT",EDGE,{"disambiguationData":[TD([[subQ2,-1.0]])],"derivedFrom":subQ1}),-1.0]])]});}
            var Q10;
            {var subQ0=sQuery(id+"F0.wireOp",EDGE,"yIff1Jyh-36eP-EJu2-z3IG-mIHMmL8X11wQ");var subQ1=sQuery(id+"F0.wireOp",EDGE,"E3");var subQ2=makeQuery(id+"F0.imprint","INTERSECT",VERTEX,{"disambiguationData":[OD(0.0)],"derivedFrom":[subQ1,subQ0]});Q10=makeQuery(id+"F0.imprint","IMPRINT",FACE,{"disambiguationData":[TD([[makeQuery(id+"F0.imprint","IMPRINT",EDGE,{"disambiguationData":[TD([[subQ2,-1.0]])],"derivedFrom":subQ1}),-1.0]])]});}
            var Q11;
            {var subQ0=sQuery(id+"F0.wireOp",EDGE,"6oBsojoL-bi50-brXo-pCNQ-iNl1vZV5s9Sy");var subQ1=sQuery(id+"F0.wireOp",EDGE,"E3");var subQ2=makeQuery(id+"F0.imprint","INTERSECT",VERTEX,{"disambiguationData":[OD(0.0)],"derivedFrom":[subQ1,subQ0]});Q11=makeQuery(id+"F0.imprint","IMPRINT",FACE,{"disambiguationData":[TD([[makeQuery(id+"F0.imprint","IMPRINT",EDGE,{"disambiguationData":[TD([[subQ2,-1.0]])],"derivedFrom":subQ1}),-1.0]])]});}
            var Q12;
            {var subQ0=sQuery(id+"F0.wireOp",EDGE,"bF5o1xas-ZAw9-uCyn-oNpS-FKpWy39mbc2z");var subQ1=sQuery(id+"F0.wireOp",EDGE,"E3");var subQ2=makeQuery(id+"F0.imprint","INTERSECT",VERTEX,{"disambiguationData":[OD(0.0)],"derivedFrom":[subQ1,subQ0]});Q12=makeQuery(id+"F0.imprint","IMPRINT",FACE,{"disambiguationData":[TD([[makeQuery(id+"F0.imprint","IMPRINT",EDGE,{"disambiguationData":[TD([[subQ2,1.0]])],"derivedFrom":subQ1}),-1.0]])]});}
            var Q13;
            {var subQ0=sQuery(id+"F0.wireOp",EDGE,"AHdYGSoF-gAz6-Gu7A-dCm8-YOlxFVZfYSgz");var subQ1=sQuery(id+"F0.wireOp",EDGE,"E3");var subQ2=makeQuery(id+"F0.imprint","INTERSECT",VERTEX,{"disambiguationData":[OD(0.0)],"derivedFrom":[subQ1,subQ0]});Q13=makeQuery(id+"F0.imprint","IMPRINT",FACE,{"disambiguationData":[TD([[makeQuery(id+"F0.imprint","IMPRINT",EDGE,{"disambiguationData":[TD([[subQ2,-1.0]])],"derivedFrom":subQ1}),-1.0]])]});}
            var Q14;
            {var subQ0=sQuery(id+"F0.wireOp",EDGE,"BIAei6Qo-JPVI-veR3-2g77-xNxDojE5xRzN");var subQ1=sQuery(id+"F0.wireOp",EDGE,"E3");var subQ2=makeQuery(id+"F0.imprint","INTERSECT",VERTEX,{"disambiguationData":[OD(0.0)],"derivedFrom":[subQ1,subQ0]});Q14=makeQuery(id+"F0.imprint","IMPRINT",FACE,{"disambiguationData":[TD([[makeQuery(id+"F0.imprint","IMPRINT",EDGE,{"disambiguationData":[TD([[subQ2,-1.0]])],"derivedFrom":subQ1}),-1.0]])]});}
            var Q15;
            {var subQ0=sQuery(id+"F0.wireOp",EDGE,"VOKNR2WF-ncJ6-5r4m-VKTM-Mp244crdFX1A");var subQ1=sQuery(id+"F0.wireOp",EDGE,"E4");var subQ2=makeQuery(id+"F0.imprint","INTERSECT",VERTEX,{"disambiguationData":[OD(0.0)],"derivedFrom":[subQ1,subQ0]});Q15=makeQuery(id+"F0.imprint","IMPRINT",FACE,{"disambiguationData":[TD([[makeQuery(id+"F0.imprint","IMPRINT",EDGE,{"disambiguationData":[TD([[subQ2,-1.0]])],"derivedFrom":subQ1}),-1.0]])]});}
            var Q16;
            {var subQ0=sQuery(id+"F0.wireOp",EDGE,"rxho1QIs-J72r-V1yP-Fany-Pfa95wKSQuel");var subQ1=sQuery(id+"F0.wireOp",EDGE,"E4");var subQ2=makeQuery(id+"F0.imprint","INTERSECT",VERTEX,{"disambiguationData":[OD(0.0)],"derivedFrom":[subQ1,subQ0]});Q16=makeQuery(id+"F0.imprint","IMPRINT",FACE,{"disambiguationData":[TD([[makeQuery(id+"F0.imprint","IMPRINT",EDGE,{"disambiguationData":[TD([[subQ2,-1.0]])],"derivedFrom":subQ1}),-1.0]])]});}
            var Q17;
            {var subQ0=sQuery(id+"F0.wireOp",EDGE,"FUVbCvpG-FZ6w-P6KP-I0dI-AxA5oCcrSkfj");var subQ1=sQuery(id+"F0.wireOp",EDGE,"E4");var subQ2=makeQuery(id+"F0.imprint","INTERSECT",VERTEX,{"disambiguationData":[OD(0.0)],"derivedFrom":[subQ1,subQ0]});Q17=makeQuery(id+"F0.imprint","IMPRINT",FACE,{"disambiguationData":[TD([[makeQuery(id+"F0.imprint","IMPRINT",EDGE,{"disambiguationData":[TD([[subQ2,-1.0]])],"derivedFrom":subQ1}),-1.0]])]});}
            var Q18;
            {var subQ0=sQuery(id+"F0.wireOp",EDGE,"RgAsl8GP-AyME-5KkZ-DOE9-8E78qrft6pB6");var subQ1=sQuery(id+"F0.wireOp",EDGE,"E4");var subQ2=makeQuery(id+"F0.imprint","INTERSECT",VERTEX,{"disambiguationData":[OD(0.0)],"derivedFrom":[subQ1,subQ0]});Q18=makeQuery(id+"F0.imprint","IMPRINT",FACE,{"disambiguationData":[TD([[makeQuery(id+"F0.imprint","IMPRINT",EDGE,{"disambiguationData":[TD([[subQ2,-1.0]])],"derivedFrom":subQ1}),-1.0]])]});}
            var Q19;
            {var subQ0=sQuery(id+"F0.wireOp",EDGE,"JKFwxpca-5GMR-r81S-5lcH-Q0wAUQQhRcdb");var subQ1=sQuery(id+"F0.wireOp",EDGE,"E4");var subQ2=makeQuery(id+"F0.imprint","INTERSECT",VERTEX,{"disambiguationData":[OD(0.0)],"derivedFrom":[subQ1,subQ0]});Q19=makeQuery(id+"F0.imprint","IMPRINT",FACE,{"disambiguationData":[TD([[makeQuery(id+"F0.imprint","IMPRINT",EDGE,{"disambiguationData":[TD([[subQ2,-1.0]])],"derivedFrom":subQ1}),-1.0]])]});}
            var Q20;
            {var subQ0=sQuery(id+"F0.wireOp",EDGE,"E58");var subQ1=sQuery(id+"F0.wireOp",EDGE,"E3");var subQ2=makeQuery(id+"F0.imprint","INTERSECT",VERTEX,{"disambiguationData":[OD(0.0)],"derivedFrom":[subQ1,subQ0]});Q20=makeQuery(id+"F0.imprint","IMPRINT",FACE,{"disambiguationData":[TD([[makeQuery(id+"F0.imprint","IMPRINT",EDGE,{"disambiguationData":[TD([[subQ2,-1.0]])],"derivedFrom":subQ1}),-1.0]])]});}
            var Q21;
            {var subQ0=sQuery(id+"F0.wireOp",EDGE,"E59");var subQ1=sQuery(id+"F0.wireOp",EDGE,"E3");var subQ2=makeQuery(id+"F0.imprint","INTERSECT",VERTEX,{"disambiguationData":[OD(0.0)],"derivedFrom":[subQ1,subQ0]});Q21=makeQuery(id+"F0.imprint","IMPRINT",FACE,{"disambiguationData":[TD([[makeQuery(id+"F0.imprint","IMPRINT",EDGE,{"disambiguationData":[TD([[subQ2,-1.0]])],"derivedFrom":subQ1}),-1.0]])]});}
            var Q22;
            {var subQ0=sQuery(id+"F0.wireOp",EDGE,"E60");var subQ1=sQuery(id+"F0.wireOp",EDGE,"E3");var subQ2=makeQuery(id+"F0.imprint","INTERSECT",VERTEX,{"disambiguationData":[OD(0.0)],"derivedFrom":[subQ1,subQ0]});Q22=makeQuery(id+"F0.imprint","IMPRINT",FACE,{"disambiguationData":[TD([[makeQuery(id+"F0.imprint","IMPRINT",EDGE,{"disambiguationData":[TD([[subQ2,1.0]])],"derivedFrom":subQ1}),-1.0]])]});}
            var Q23;
            {var subQ0=sQuery(id+"F0.wireOp",EDGE,"E61");var subQ1=sQuery(id+"F0.wireOp",EDGE,"E3");var subQ2=makeQuery(id+"F0.imprint","INTERSECT",VERTEX,{"disambiguationData":[OD(0.0)],"derivedFrom":[subQ1,subQ0]});Q23=makeQuery(id+"F0.imprint","IMPRINT",FACE,{"disambiguationData":[TD([[makeQuery(id+"F0.imprint","IMPRINT",EDGE,{"disambiguationData":[TD([[subQ2,-1.0]])],"derivedFrom":subQ1}),-1.0]])]});}
            var Q24;
            {var subQ0=sQuery(id+"F0.wireOp",EDGE,"E62");var subQ1=sQuery(id+"F0.wireOp",EDGE,"E3");var subQ2=makeQuery(id+"F0.imprint","INTERSECT",VERTEX,{"disambiguationData":[OD(0.0)],"derivedFrom":[subQ1,subQ0]});Q24=makeQuery(id+"F0.imprint","IMPRINT",FACE,{"disambiguationData":[TD([[makeQuery(id+"F0.imprint","IMPRINT",EDGE,{"disambiguationData":[TD([[subQ2,-1.0]])],"derivedFrom":subQ1}),-1.0]])]});}
            var Q25;
            {var subQ0=sQuery(id+"F0.wireOp",EDGE,"E72");var subQ1=sQuery(id+"F0.wireOp",EDGE,"E4");var subQ2=makeQuery(id+"F0.imprint","INTERSECT",VERTEX,{"disambiguationData":[OD(0.0)],"derivedFrom":[subQ1,subQ0]});Q25=makeQuery(id+"F0.imprint","IMPRINT",FACE,{"disambiguationData":[TD([[makeQuery(id+"F0.imprint","IMPRINT",EDGE,{"disambiguationData":[TD([[subQ2,-1.0]])],"derivedFrom":subQ1}),-1.0]])]});}
            var Q26;
            {var subQ0=sQuery(id+"F0.wireOp",EDGE,"E68");var subQ1=sQuery(id+"F0.wireOp",EDGE,"E4");var subQ2=makeQuery(id+"F0.imprint","INTERSECT",VERTEX,{"disambiguationData":[OD(0.0)],"derivedFrom":[subQ1,subQ0]});Q26=makeQuery(id+"F0.imprint","IMPRINT",FACE,{"disambiguationData":[TD([[makeQuery(id+"F0.imprint","IMPRINT",EDGE,{"disambiguationData":[TD([[subQ2,-1.0]])],"derivedFrom":subQ1}),-1.0]])]});}
            var Q27;
            {var subQ0=sQuery(id+"F0.wireOp",EDGE,"E69");var subQ1=sQuery(id+"F0.wireOp",EDGE,"E4");var subQ2=makeQuery(id+"F0.imprint","INTERSECT",VERTEX,{"disambiguationData":[OD(0.0)],"derivedFrom":[subQ1,subQ0]});Q27=makeQuery(id+"F0.imprint","IMPRINT",FACE,{"disambiguationData":[TD([[makeQuery(id+"F0.imprint","IMPRINT",EDGE,{"disambiguationData":[TD([[subQ2,-1.0]])],"derivedFrom":subQ1}),-1.0]])]});}
            var Q28;
            {var subQ0=sQuery(id+"F0.wireOp",EDGE,"E70");var subQ1=sQuery(id+"F0.wireOp",EDGE,"E4");var subQ2=makeQuery(id+"F0.imprint","INTERSECT",VERTEX,{"disambiguationData":[OD(0.0)],"derivedFrom":[subQ1,subQ0]});Q28=makeQuery(id+"F0.imprint","IMPRINT",FACE,{"disambiguationData":[TD([[makeQuery(id+"F0.imprint","IMPRINT",EDGE,{"disambiguationData":[TD([[subQ2,-1.0]])],"derivedFrom":subQ1}),-1.0]])]});}
            var Q29;
            {var subQ0=sQuery(id+"F0.wireOp",EDGE,"E71");var subQ1=sQuery(id+"F0.wireOp",EDGE,"E4");var subQ2=makeQuery(id+"F0.imprint","INTERSECT",VERTEX,{"disambiguationData":[OD(0.0)],"derivedFrom":[subQ1,subQ0]});Q29=makeQuery(id+"F0.imprint","IMPRINT",FACE,{"disambiguationData":[TD([[makeQuery(id+"F0.imprint","IMPRINT",EDGE,{"disambiguationData":[TD([[subQ2,-1.0]])],"derivedFrom":subQ1}),-1.0]])]});}
            extrude(context, id + "F2", {"entities" : qUnion([Q0, Q1, Q2, Q3, Q4, Q5, Q6, Q7, Q8, Q9, Q10, Q11, Q12, Q13, Q14, Q15, Q16, Q17, Q18, Q19, Q20, Q21, Q22, Q23, Q24, Q25, Q26, Q27, Q28, Q29]), "operationType" : NewBodyOperationType.REMOVE, "depth" : 2 * mm, "offsetDistance" : 25 * mm});
        }
        {
            var Q0;
            Q0=makeQuery(id+"F0.imprint","IMPRINT",FACE,{"disambiguationData":[TD([[makeQuery(id+"F0.imprint","IMPRINT",EDGE,{"derivedFrom":sQuery(id+"F0.wireOp",EDGE,"E22")}),-1.0]])]});
            var Q1;
            Q1=makeQuery(id+"F0.imprint","IMPRINT",FACE,{"disambiguationData":[TD([[makeQuery(id+"F0.imprint","IMPRINT",EDGE,{"derivedFrom":sQuery(id+"F0.wireOp",EDGE,"E18")}),-1.0]])]});
            var Q2;
            Q2=makeQuery(id+"F0.imprint","IMPRINT",FACE,{"disambiguationData":[TD([[makeQuery(id+"F0.imprint","IMPRINT",EDGE,{"derivedFrom":sQuery(id+"F0.wireOp",EDGE,"E21")}),-1.0]])]});
            extrude(context, id + "F3", {"entities" : qUnion([Q0, Q1, Q2]), "operationType" : NewBodyOperationType.REMOVE, "depth" : 3 * mm, "offsetDistance" : 25 * mm});
        }
        {
            var Q0;
            Q0=makeQuery(id+"F0.imprint","IMPRINT",FACE,{"disambiguationData":[TD([[makeQuery(id+"F0.imprint","IMPRINT",EDGE,{"derivedFrom":sQuery(id+"F0.wireOp",EDGE,"E22")}),-1.0]])]});
            var Q1;
            Q1=makeQuery(id+"F0.imprint","IMPRINT",FACE,{"disambiguationData":[TD([[makeQuery(id+"F0.imprint","IMPRINT",EDGE,{"derivedFrom":sQuery(id+"F0.wireOp",EDGE,"E18")}),-1.0]])]});
            var Q2;
            Q2=makeQuery(id+"F0.imprint","IMPRINT",FACE,{"disambiguationData":[TD([[makeQuery(id+"F0.imprint","IMPRINT",EDGE,{"derivedFrom":sQuery(id+"F0.wireOp",EDGE,"E21")}),-1.0]])]});
            extrude(context, id + "F4", {"entities" : qUnion([Q0, Q1, Q2]), "operationType" : NewBodyOperationType.ADD, "depth" : 1.5 * mm, "offsetDistance" : 25 * mm});
        }
        {
            var Q0;
            Q0=makeQuery(id+"F1.opExtrude","CAP_EDGE",EDGE,{"disambiguationData":[OSD([sQuery(id+"F0.wireOp",EDGE,"E0.left")])],"isStart":false});
            var Q1;
            Q1=makeQuery(id+"F1.opExtrude","SWEPT_EDGE",EDGE,{"disambiguationData":[OSD([sQuery(id+"F0.wireOp",EDGE,"E0.bottom"),sQuery(id+"F0.wireOp",EDGE,"E0.left")])]});
            var Q2;
            Q2=makeQuery(id+"F1.opExtrude","CAP_EDGE",EDGE,{"disambiguationData":[OSD([sQuery(id+"F0.wireOp",EDGE,"E0.bottom")])],"isStart":false});
            var Q3;
            Q3=makeQuery(id+"F1.opExtrude","CAP_EDGE",EDGE,{"disambiguationData":[OSD([sQuery(id+"F0.wireOp",EDGE,"E0.top")])],"isStart":false});
            var Q4;
            Q4=makeQuery(id+"F1.opExtrude","SWEPT_EDGE",EDGE,{"disambiguationData":[OSD([sQuery(id+"F0.wireOp",EDGE,"E0.top"),sQuery(id+"F0.wireOp",EDGE,"E0.right")])]});
            var Q5;
            Q5=makeQuery(id+"F1.opExtrude","CAP_EDGE",EDGE,{"disambiguationData":[OSD([sQuery(id+"F0.wireOp",EDGE,"E0.right")])],"isStart":false});
            var Q6;
            Q6=makeQuery(id+"F1.opExtrude","SWEPT_EDGE",EDGE,{"disambiguationData":[OSD([sQuery(id+"F0.wireOp",EDGE,"E0.bottom"),sQuery(id+"F0.wireOp",EDGE,"E0.right")])]});
            var Q7;
            Q7=makeQuery(id+"F1.opExtrude","SWEPT_EDGE",EDGE,{"disambiguationData":[OSD([sQuery(id+"F0.wireOp",EDGE,"E0.top"),sQuery(id+"F0.wireOp",EDGE,"E0.left")])]});
            fillet(context, id + "F5", {"entities" : qUnion([Q0, Q1, Q2, Q3, Q4, Q5, Q6, Q7]), "radius" : 1 * mm, "tangentPropagation" : true, "allowEdgeOverflow" : false});
        }
        {
            var Q0;
            Q0=makeQuery(id+"F1.opExtrude","CAP_EDGE",EDGE,{"disambiguationData":[OSD([sQuery(id+"F0.wireOp",EDGE,"E4")])],"isStart":false});
            var Q1;
            Q1=makeQuery(id+"F1.opExtrude","CAP_EDGE",EDGE,{"disambiguationData":[OSD([sQuery(id+"F0.wireOp",EDGE,"E14"),sQuery(id+"F0.wireOp",EDGE,"E16")])],"isStart":false});
            var Q2;
            Q2=makeQuery(id+"F1.opExtrude","CAP_EDGE",EDGE,{"disambiguationData":[OSD([sQuery(id+"F0.wireOp",EDGE,"E15")])],"isStart":false});
            var Q3;
            Q3=makeQuery(id+"F1.opExtrude","CAP_EDGE",EDGE,{"disambiguationData":[OSD([sQuery(id+"F0.wireOp",EDGE,"E17")])],"isStart":false});
            var Q4;
            Q4=makeQuery(id+"F1.opExtrude","CAP_EDGE",EDGE,{"disambiguationData":[OSD([sQuery(id+"F0.wireOp",EDGE,"E3")])],"isStart":false});
            var Q5;
            Q5=makeQuery(id+"F1.opExtrude","CAP_EDGE",EDGE,{"disambiguationData":[OSD([sQuery(id+"F0.wireOp",EDGE,"E11")])],"isStart":false});
            var Q6;
            Q6=makeQuery(id+"F1.opExtrude","CAP_EDGE",EDGE,{"disambiguationData":[OSD([sQuery(id+"F0.wireOp",EDGE,"E12")])],"isStart":false});
            var Q7;
            Q7=makeQuery(id+"F1.opExtrude","CAP_EDGE",EDGE,{"disambiguationData":[OSD([sQuery(id+"F0.wireOp",EDGE,"E9"),sQuery(id+"F0.wireOp",EDGE,"E10")])],"isStart":false});
            fillet(context, id + "F6", {"entities" : qUnion([Q0, Q1, Q2, Q3, Q4, Q5, Q6, Q7]), "radius" : .5 * mm, "tangentPropagation" : true, "allowEdgeOverflow" : false});
        }
        {
            var Q0;
            Q0=makeQuery(id+"F1.opExtrude","SWEPT_EDGE",EDGE,{"disambiguationData":[OSD([sQuery(id+"F0.wireOp",EDGE,"E9"),sQuery(id+"F0.wireOp",EDGE,"E11")])]});
            var Q1;
            Q1=makeQuery(id+"F1.opExtrude","SWEPT_EDGE",EDGE,{"disambiguationData":[OSD([sQuery(id+"F0.wireOp",EDGE,"E14"),sQuery(id+"F0.wireOp",EDGE,"E15")])]});
            var Q2;
            Q2=makeQuery(id+"F1.opExtrude","SWEPT_EDGE",EDGE,{"disambiguationData":[OSD([sQuery(id+"F0.wireOp",EDGE,"E16"),sQuery(id+"F0.wireOp",EDGE,"E17")])]});
            var Q3;
            Q3=makeQuery(id+"F1.opExtrude","SWEPT_EDGE",EDGE,{"disambiguationData":[OSD([sQuery(id+"F0.wireOp",EDGE,"E10"),sQuery(id+"F0.wireOp",EDGE,"E12")])]});
            fillet(context, id + "F7", {"entities" : qUnion([Q0, Q1, Q2, Q3]), "radius" : 1 * mm, "tangentPropagation" : true, "allowEdgeOverflow" : false});
        }
        {
            var Q0;
            Q0=makeQuery(id+"F2.boolean.opBoolean","COPY",EDGE,{"derivedFrom":makeQuery(id+"F2.opExtrude","CAP_EDGE",EDGE,{"disambiguationData":[OSD([sQuery(id+"F0.wireOp",EDGE,"E58")])],"isStart":false})});
            var Q1;
            Q1=makeQuery(id+"F2.boolean.opBoolean","COPY",EDGE,{"derivedFrom":makeQuery(id+"F2.opExtrude","CAP_EDGE",EDGE,{"disambiguationData":[OSD([sQuery(id+"F0.wireOp",EDGE,"E62")])],"isStart":false})});
            var Q2;
            Q2=makeQuery(id+"F2.boolean.opBoolean","COPY",EDGE,{"derivedFrom":makeQuery(id+"F2.opExtrude","CAP_EDGE",EDGE,{"disambiguationData":[OSD([sQuery(id+"F0.wireOp",EDGE,"E61")])],"isStart":false})});
            var Q3;
            Q3=makeQuery(id+"F2.boolean.opBoolean","COPY",EDGE,{"derivedFrom":makeQuery(id+"F2.opExtrude","CAP_EDGE",EDGE,{"disambiguationData":[OSD([sQuery(id+"F0.wireOp",EDGE,"E59")])],"isStart":false})});
            var Q4;
            Q4=makeQuery(id+"F2.boolean.opBoolean","COPY",EDGE,{"derivedFrom":makeQuery(id+"F2.opExtrude","CAP_EDGE",EDGE,{"disambiguationData":[OSD([sQuery(id+"F0.wireOp",EDGE,"E60")])],"isStart":false})});
            var Q5;
            Q5=makeQuery(id+"F2.boolean.opBoolean","COPY",EDGE,{"derivedFrom":makeQuery(id+"F2.opExtrude","CAP_EDGE",EDGE,{"disambiguationData":[OSD([sQuery(id+"F0.wireOp",EDGE,"E69")])],"isStart":false})});
            var Q6;
            Q6=makeQuery(id+"F2.boolean.opBoolean","COPY",EDGE,{"derivedFrom":makeQuery(id+"F2.opExtrude","CAP_EDGE",EDGE,{"disambiguationData":[OSD([sQuery(id+"F0.wireOp",EDGE,"E70")])],"isStart":false})});
            var Q7;
            Q7=makeQuery(id+"F2.boolean.opBoolean","COPY",EDGE,{"derivedFrom":makeQuery(id+"F2.opExtrude","CAP_EDGE",EDGE,{"disambiguationData":[OSD([sQuery(id+"F0.wireOp",EDGE,"E68")])],"isStart":false})});
            var Q8;
            Q8=makeQuery(id+"F2.boolean.opBoolean","COPY",EDGE,{"derivedFrom":makeQuery(id+"F2.opExtrude","CAP_EDGE",EDGE,{"disambiguationData":[OSD([sQuery(id+"F0.wireOp",EDGE,"E72")])],"isStart":false})});
            var Q9;
            Q9=makeQuery(id+"F2.boolean.opBoolean","COPY",EDGE,{"derivedFrom":makeQuery(id+"F2.opExtrude","CAP_EDGE",EDGE,{"disambiguationData":[OSD([sQuery(id+"F0.wireOp",EDGE,"E71")])],"isStart":false})});
            fillet(context, id + "F8", {"entities" : qUnion([Q0, Q1, Q2, Q3, Q4, Q5, Q6, Q7, Q8, Q9]), "radius" : 1.2 * mm, "tangentPropagation" : true, "allowEdgeOverflow" : false});
        }
    });
